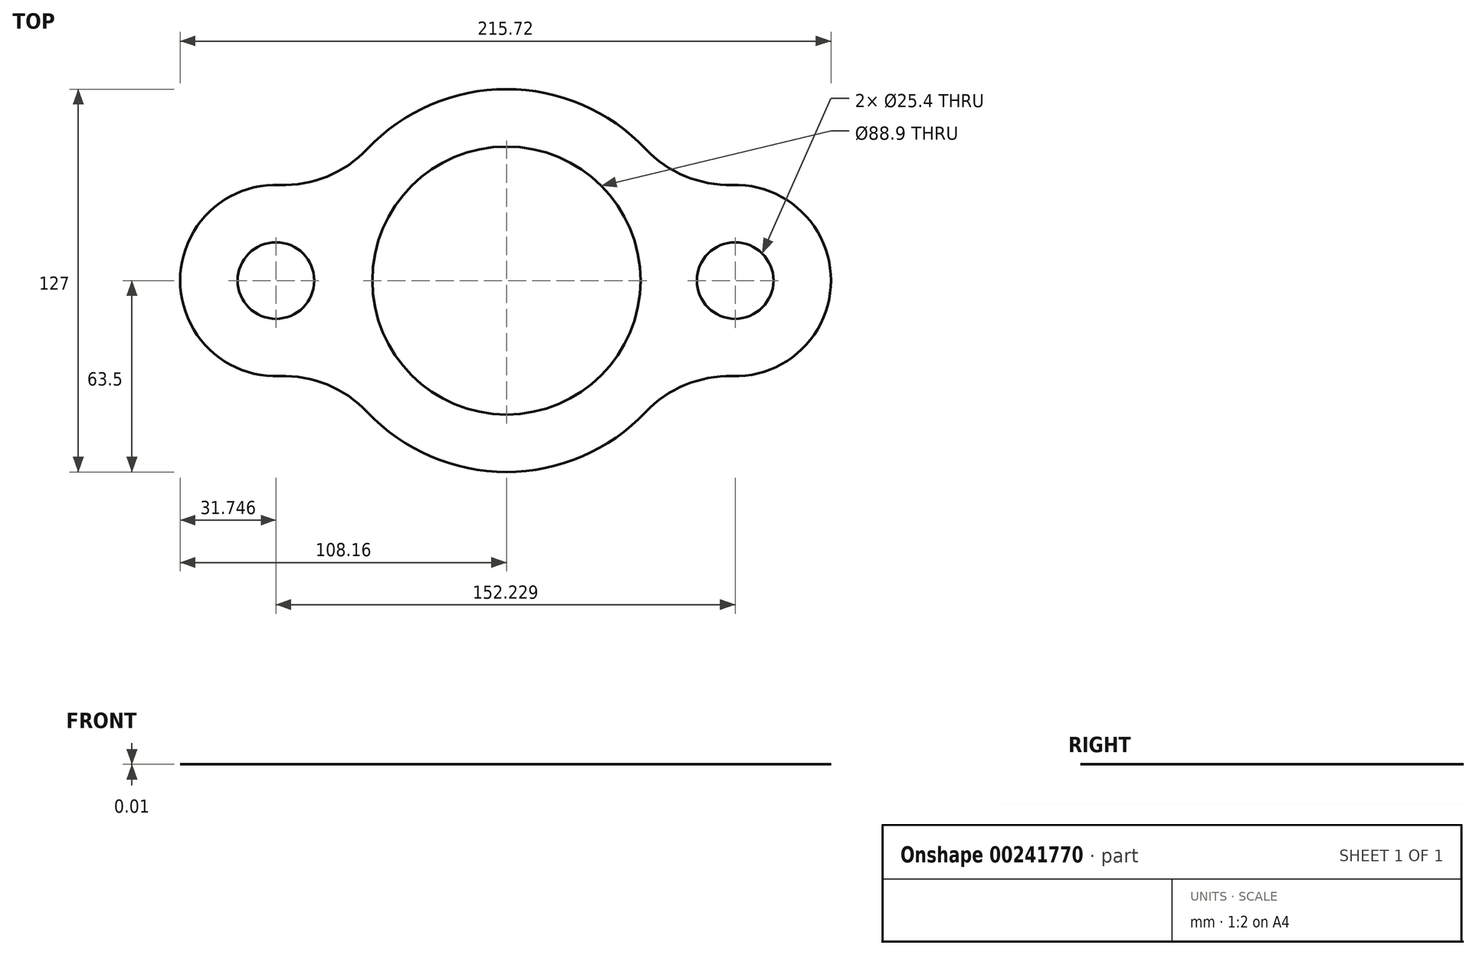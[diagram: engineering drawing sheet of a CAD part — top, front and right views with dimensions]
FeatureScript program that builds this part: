
annotation { "Feature Type Name" : "Feature", "Feature Type Description" : "" }
export const myFeature = defineFeature(function(context is Context, id is Id, definition is map)
    precondition{}
    {
        {
            var Q0;
            Q0=qCreatedBy(makeId("Top.planeOp"),FACE);
            var sketch = newSketch(context, id + "F0", { "sketchPlane" : qUnion([Q0])});
            skCircle(sketch, "E0", {"center": v(0, 0) * mm, "radius": 44.45 * mm});
            skCircle(sketch, "E1", {"center": v(-76.41, 0) * mm, "radius": 12.7 * mm});
            skCircle(sketch, "E2", {"center": v(75.81, 0) * mm, "radius": 12.7 * mm});
            skCircle(sketch, "E3", {"center": v(0, 0) * mm, "radius": 63.5 * mm});
            skCircle(sketch, "E4", {"center": v(-76.41, 0) * mm, "radius": 31.75 * mm});
            skCircle(sketch, "E5", {"center": v(75.81, 0) * mm, "radius": 31.75 * mm});
            skSolve(sketch);
        }
        {
            var Q0;
            Q0 = qSketchRegion(id + "F0", true);
            extrude(context, id + "F1", {"entities" : qUnion([Q0]), "depth" : 1 / 101.6 * mm});
        }
        {
            var Q0;
            {var subQ0=sQuery(id+"F0.wireOp",EDGE,"E4");var subQ1=sQuery(id+"F0.wireOp",EDGE,"E3");Q0=makeQuery(id+"F1.opExtrude","SWEPT_EDGE",EDGE,{"disambiguationData":[OSD([subQ1,subQ0]),TDD([makeQuery(id+"F0.imprint","INTERSECT",VERTEX,{"disambiguationData":[OD(0.0)],"derivedFrom":[subQ1,subQ0]})])]});}
            var Q1;
            {var subQ0=sQuery(id+"F0.wireOp",EDGE,"E5");var subQ1=sQuery(id+"F0.wireOp",EDGE,"E3");Q1=makeQuery(id+"F1.opExtrude","SWEPT_EDGE",EDGE,{"disambiguationData":[OSD([subQ1,subQ0]),TDD([makeQuery(id+"F0.imprint","INTERSECT",VERTEX,{"disambiguationData":[OD(0.0)],"derivedFrom":[subQ1,subQ0]})])]});}
            var Q2;
            {var subQ0=sQuery(id+"F0.wireOp",EDGE,"E4");var subQ1=sQuery(id+"F0.wireOp",EDGE,"E3");Q2=makeQuery(id+"F1.opExtrude","SWEPT_EDGE",EDGE,{"disambiguationData":[OSD([subQ1,subQ0]),TDD([makeQuery(id+"F0.imprint","INTERSECT",VERTEX,{"disambiguationData":[OD(1.0)],"derivedFrom":[subQ1,subQ0]})])]});}
            var Q3;
            {var subQ0=sQuery(id+"F0.wireOp",EDGE,"E5");var subQ1=sQuery(id+"F0.wireOp",EDGE,"E3");Q3=makeQuery(id+"F1.opExtrude","SWEPT_EDGE",EDGE,{"disambiguationData":[OSD([subQ1,subQ0]),TDD([makeQuery(id+"F0.imprint","INTERSECT",VERTEX,{"disambiguationData":[OD(1.0)],"derivedFrom":[subQ1,subQ0]})])]});}
            fillet(context, id + "F2", {"entities" : qUnion([Q0, Q1, Q2, Q3]), "radius" : 38.1 * mm, "tangentPropagation" : true, "allowEdgeOverflow" : false});
        }
    });
